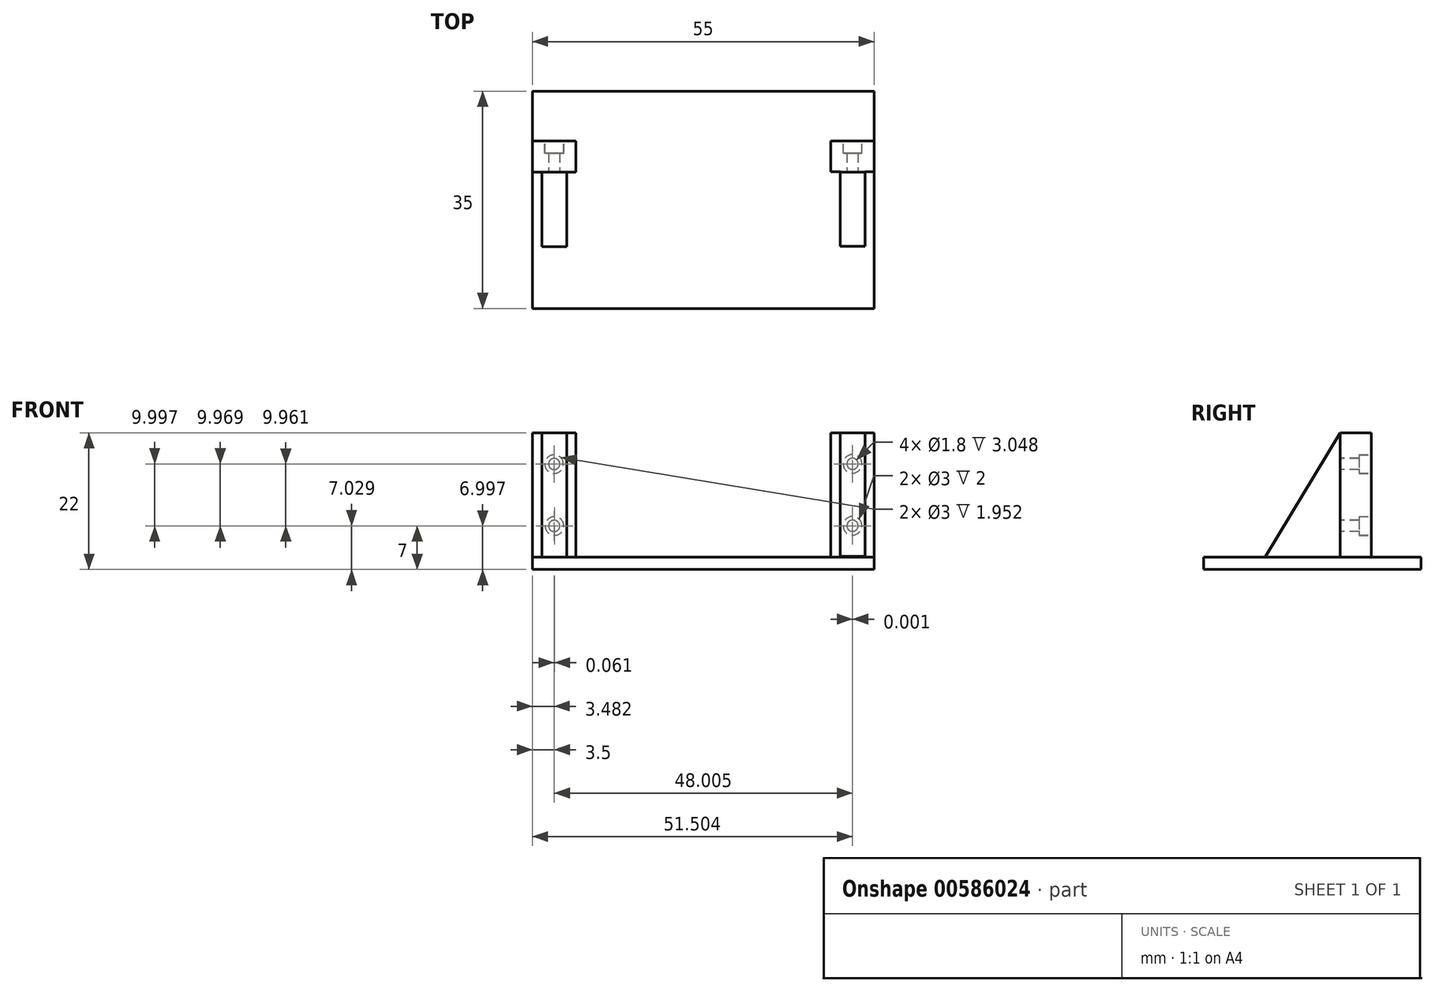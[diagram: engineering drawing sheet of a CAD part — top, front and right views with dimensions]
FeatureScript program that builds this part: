
annotation { "Feature Type Name" : "Feature", "Feature Type Description" : "" }
export const myFeature = defineFeature(function(context is Context, id is Id, definition is map)
    precondition{}
    {
        {
            var Q0;
            Q0=qCreatedBy(makeId("Top.planeOp"),FACE);
            var sketch = newSketch(context, id + "F0", { "sketchPlane" : qUnion([Q0])});
            skLineSegment(sketch, "E0.bottom", {"start": v(-27.5, 17.5) * mm, "end": v(27.5, 17.5) * mm});
            skLineSegment(sketch, "E0.top", {"start": v(-27.5, -17.5) * mm, "end": v(27.5, -17.5) * mm});
            skLineSegment(sketch, "E0.left", {"start": v(-27.5, 17.5) * mm, "end": v(-27.5, -17.5) * mm});
            skLineSegment(sketch, "E0.right", {"start": v(27.5, 17.5) * mm, "end": v(27.5, -17.5) * mm});
            skPoint(sketch, "E0.middle", {"position": v(0, 0) * mm});
            skSolve(sketch);
        }
        {
            var Q0;
            Q0=makeQuery(id+"F0.imprint","IMPRINT",FACE,{"disambiguationData":[TD([[makeQuery(id+"F0.imprint","IMPRINT",EDGE,{"derivedFrom":sQuery(id+"F0.wireOp",EDGE,"E0.bottom")}),-1.0]])]});
            extrude(context, id + "F1", {"entities" : qUnion([Q0]), "depth" : 2 * mm, "offsetDistance" : 25 * mm});
        }
        {
            var Q0;
            Q0=makeQuery(id+"F1.opExtrude","CAP_FACE",FACE,{"disambiguationData":[OSD([sQuery(id+"F0.wireOp",EDGE,"E0.bottom"),sQuery(id+"F0.wireOp",EDGE,"E0.top"),sQuery(id+"F0.wireOp",EDGE,"E0.left"),sQuery(id+"F0.wireOp",EDGE,"E0.right")])],"isStart":false});
            var sketch = newSketch(context, id + "F2", { "sketchPlane" : qUnion([Q0])});
            skLineSegment(sketch, "E1", {"start": v(-27.5, 9.5) * mm, "end": v(27.5, 9.5) * mm, "construction": true});
            skLineSegment(sketch, "E2", {"start": v(20.5, 17.5) * mm, "end": v(20.5, -17.5) * mm, "construction": true});
            skLineSegment(sketch, "E3", {"start": v(-20.5, 17.5) * mm, "end": v(-20.5, -17.5) * mm, "construction": true});
            skSolve(sketch);
        }
        {
            var Q0;
            Q0=makeQuery(id+"F2.imprint","IMPRINT",FACE,{"disambiguationData":[TD([[makeQuery(id+"F2.imprint","IMPRINT",EDGE,{"derivedFrom":makeQuery(id+"F1.opExtrude","CAP_EDGE",EDGE,{"disambiguationData":[OSD([sQuery(id+"F0.wireOp",EDGE,"E0.bottom")])],"isStart":false})}),-1.0]])]});
            var sketch = newSketch(context, id + "F3", { "sketchPlane" : qUnion([Q0])});
            skLineSegment(sketch, "E4.bottom", {"start": v(20.5, 9.5) * mm, "end": v(27.5, 9.5) * mm});
            skLineSegment(sketch, "E4.top", {"start": v(20.5, 4.5) * mm, "end": v(27.5, 4.5) * mm});
            skLineSegment(sketch, "E4.left", {"start": v(20.5, 9.5) * mm, "end": v(20.5, 4.5) * mm});
            skLineSegment(sketch, "E4.right", {"start": v(27.5, 9.5) * mm, "end": v(27.5, 4.5) * mm});
            skLineSegment(sketch, "E5.bottom", {"start": v(-27.5, 9.45) * mm, "end": v(-20.5, 9.45) * mm});
            skLineSegment(sketch, "E5.top", {"start": v(-27.5, 4.45) * mm, "end": v(-20.5, 4.45) * mm});
            skLineSegment(sketch, "E5.left", {"start": v(-27.5, 9.5) * mm, "end": v(-27.5, 4.45) * mm});
            skLineSegment(sketch, "E5.right", {"start": v(-20.5, 9.45) * mm, "end": v(-20.5, 4.45) * mm});
            skLineSegment(sketch, "E6.bottom", {"start": v(-22, -7.55) * mm, "end": v(-26, -7.55) * mm});
            skLineSegment(sketch, "E6.top", {"start": v(-22, 4.45) * mm, "end": v(-26, 4.45) * mm});
            skLineSegment(sketch, "E6.left", {"start": v(-22, -7.55) * mm, "end": v(-22, 4.45) * mm});
            skLineSegment(sketch, "E6.right", {"start": v(-26, -7.55) * mm, "end": v(-26, 4.45) * mm});
            skPoint(sketch, "E6.middle", {"position": v(-24, -1.55) * mm});
            skLineSegment(sketch, "E7", {"start": v(-24, 4.45) * mm, "end": v(-24, -7.55) * mm, "construction": true});
            skLineSegment(sketch, "E8", {"start": v(-24, 9.45) * mm, "end": v(-24, 4.45) * mm, "construction": true});
            skLineSegment(sketch, "E9", {"start": v(24, 9.5) * mm, "end": v(24, 4.5) * mm, "construction": true});
            skLineSegment(sketch, "E10.bottom", {"start": v(26, -7.5) * mm, "end": v(22, -7.5) * mm});
            skLineSegment(sketch, "E10.top", {"start": v(26, 4.5) * mm, "end": v(22, 4.5) * mm});
            skLineSegment(sketch, "E10.left", {"start": v(26, -7.5) * mm, "end": v(26, 4.5) * mm});
            skLineSegment(sketch, "E10.right", {"start": v(22, -7.5) * mm, "end": v(22, 4.5) * mm});
            skPoint(sketch, "E10.middle", {"position": v(24, -1.5) * mm});
            skLineSegment(sketch, "E11", {"start": v(24, 4.5) * mm, "end": v(24, -7.5) * mm, "construction": true});
            skSolve(sketch);
        }
        {
            var Q0;
            Q0=makeQuery(id+"F3.imprint","IMPRINT",FACE,{"disambiguationData":[TD([[makeQuery(id+"F3.imprint","IMPRINT",EDGE,{"derivedFrom":sQuery(id+"F3.wireOp",EDGE,"E5.bottom")}),-1.0]])]});
            var Q1;
            Q1=makeQuery(id+"F3.imprint","IMPRINT",FACE,{"disambiguationData":[TD([[makeQuery(id+"F3.imprint","IMPRINT",EDGE,{"derivedFrom":sQuery(id+"F3.wireOp",EDGE,"E4.bottom")}),-1.0]])]});
            var Q2;
            Q2=makeQuery(id+"F3.imprint","IMPRINT",FACE,{"disambiguationData":[TD([[makeQuery(id+"F3.imprint","IMPRINT",EDGE,{"derivedFrom":sQuery(id+"F3.wireOp",EDGE,"E6.bottom")}),-1.0]])]});
            var Q3;
            Q3=makeQuery(id+"F3.imprint","IMPRINT",FACE,{"disambiguationData":[TD([[makeQuery(id+"F3.imprint","IMPRINT",EDGE,{"derivedFrom":sQuery(id+"F3.wireOp",EDGE,"E10.bottom")}),-1.0]])]});
            extrude(context, id + "F4", {"entities" : qUnion([Q0, Q1, Q2, Q3]), "depth" : 20 * mm, "offsetDistance" : 25 * mm});
        }
        {
            var Q0;
            Q0=makeQuery(id+"F4.opExtrude","SWEPT_FACE",FACE,{"disambiguationData":[OSD([sQuery(id+"F3.wireOp",EDGE,"E5.top")])]});
            var sketch = newSketch(context, id + "F5", { "sketchPlane" : qUnion([Q0])});
            skLineSegment(sketch, "E12", {"start": v(-27.5, 7) * mm, "end": v(27.56, 7) * mm, "construction": true});
            skLineSegment(sketch, "E13", {"start": v(-27.5, 17) * mm, "end": v(27.47, 17) * mm, "construction": true});
            skLineSegment(sketch, "E14", {"start": v(-24, 1.81) * mm, "end": v(-24, 22) * mm, "construction": true});
            skLineSegment(sketch, "E15", {"start": v(24.08, 2.05) * mm, "end": v(24.08, 22.14) * mm, "construction": true});
            skSolve(sketch);
        }
        {
            var Q0;
            {var subQ0=sQuery(id+"F3.wireOp",EDGE,"E5.top");Q0=makeQuery(id+"F5.imprint","IMPRINT",FACE,{"disambiguationData":[TD([[makeQuery(id+"F5.imprint","IMPRINT",EDGE,{"derivedFrom":makeQuery(id+"F4.opExtrude","CAP_EDGE",EDGE,{"disambiguationData":[OSD([subQ0])],"isStart":true})}),1.0]])]});}
            var sketch = newSketch(context, id + "F6", { "sketchPlane" : qUnion([Q0])});
            skCircle(sketch, "E16", {"center": v(-24, 16.99) * mm, "radius": 0.9 * mm});
            skCircle(sketch, "E17", {"center": v(-24, 7) * mm, "radius": 0.9 * mm});
            skCircle(sketch, "E18", {"center": v(24, 17) * mm, "radius": 0.9 * mm});
            skCircle(sketch, "E19", {"center": v(24, 7.03) * mm, "radius": 0.9 * mm});
            skSolve(sketch);
        }
        {
            var Q0;
            Q0 = qSketchRegion(id + "F6", true);
            extrude(context, id + "F7", {"entities" : qUnion([Q0]), "operationType" : NewBodyOperationType.REMOVE, "oppositeDirection" : true, "depth" : 7 * mm, "offsetDistance" : 25 * mm});
        }
        {
            var Q0;
            Q0=makeQuery(id+"F4.opExtrude","SWEPT_FACE",FACE,{"disambiguationData":[OSD([sQuery(id+"F3.wireOp",EDGE,"E4.bottom")])]});
            var sketch = newSketch(context, id + "F8", { "sketchPlane" : qUnion([Q0])});
            skCircle(sketch, "E20", {"center": v(-24, 17) * mm, "radius": 1.5 * mm});
            skCircle(sketch, "E21", {"center": v(-24, 7.03) * mm, "radius": 1.5 * mm});
            skCircle(sketch, "E22", {"center": v(24.02, 16.96) * mm, "radius": 1.5 * mm});
            skCircle(sketch, "E23", {"center": v(23.96, 7) * mm, "radius": 1.5 * mm});
            skSolve(sketch);
        }
        {
            var Q0;
            Q0=makeQuery(id+"F8.imprint","IMPRINT",FACE,{"disambiguationData":[TD([[makeQuery(id+"F8.imprint","IMPRINT",EDGE,{"derivedFrom":sQuery(id+"F8.wireOp",EDGE,"E20")}),1.0]])]});
            var Q1;
            Q1=makeQuery(id+"F8.imprint","IMPRINT",FACE,{"disambiguationData":[TD([[makeQuery(id+"F8.imprint","IMPRINT",EDGE,{"derivedFrom":sQuery(id+"F8.wireOp",EDGE,"E21")}),1.0]])]});
            var Q2;
            Q2=makeQuery(id+"F8.imprint","IMPRINT",FACE,{"disambiguationData":[TD([[makeQuery(id+"F8.imprint","IMPRINT",EDGE,{"derivedFrom":sQuery(id+"F8.wireOp",EDGE,"E22")}),1.0]])]});
            var Q3;
            Q3=makeQuery(id+"F8.imprint","IMPRINT",FACE,{"disambiguationData":[TD([[makeQuery(id+"F8.imprint","IMPRINT",EDGE,{"derivedFrom":sQuery(id+"F8.wireOp",EDGE,"E23")}),1.0]])]});
            extrude(context, id + "F9", {"entities" : qUnion([Q0, Q1, Q2, Q3]), "operationType" : NewBodyOperationType.REMOVE, "oppositeDirection" : true, "depth" : 2 * mm, "offsetDistance" : 25 * mm});
        }
        {
            var Q0;
            Q0=makeQuery(id+"F4.opExtrude","SWEPT_FACE",FACE,{"disambiguationData":[OSD([sQuery(id+"F3.wireOp",EDGE,"E6.right")])]});
            var sketch = newSketch(context, id + "F10", { "sketchPlane" : qUnion([Q0])});
            skLineSegment(sketch, "E24", {"start": v(7.55, 2) * mm, "end": v(-4.45, 22) * mm});
            skSolve(sketch);
        }
        {
            var Q0;
            Q0 = qSketchRegion(id + "F10", true);
            var Q1;
            Q1=makeQuery(id+"F10.imprint","IMPRINT",FACE,{"disambiguationData":[TD([[makeQuery(id+"F10.imprint","IMPRINT",EDGE,{"derivedFrom":sQuery(id+"F10.wireOp",EDGE,"E24")}),-1.0]])]});
            extrude(context, id + "F11", {"entities" : qUnion([Q0, Q1]), "operationType" : NewBodyOperationType.REMOVE, "oppositeDirection" : true, "depth" : 55 * mm, "offsetDistance" : 25 * mm});
        }
    });
